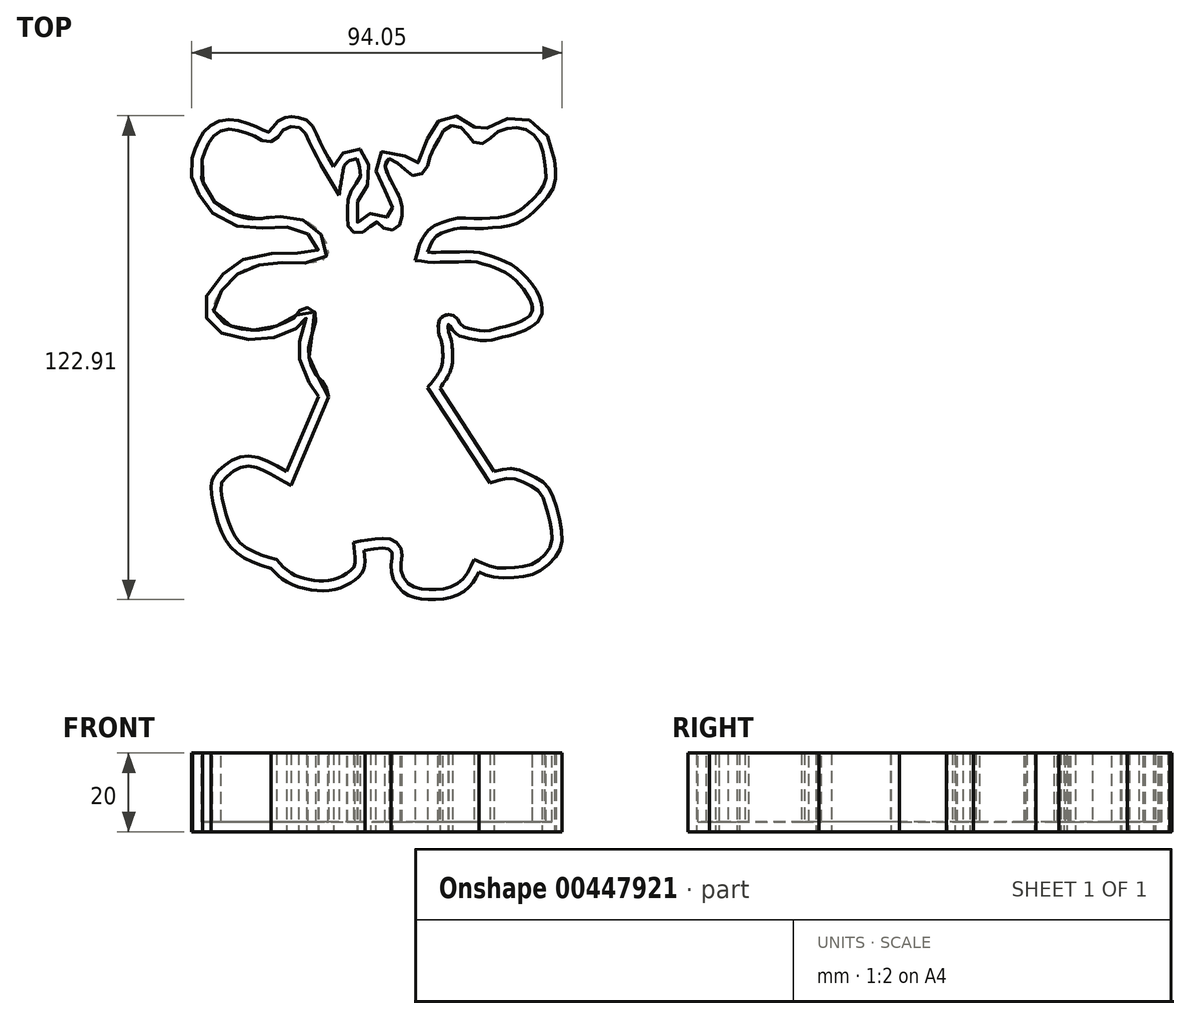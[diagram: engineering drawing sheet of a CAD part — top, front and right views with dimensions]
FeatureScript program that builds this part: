
annotation { "Feature Type Name" : "Feature", "Feature Type Description" : "" }
export const myFeature = defineFeature(function(context is Context, id is Id, definition is map)
    precondition{}
    {
        {
            var Q0;
            Q0=qCreatedBy(makeId("Top.planeOp"),FACE);
            var sketch = newSketch(context, id + "F0", { "sketchPlane" : qUnion([Q0])});
            skLineSegment(sketch, "E0", {"start": v(9.16, -14.18) * mm, "end": v(22.95, -35.4) * mm});
            skLineSegment(sketch, "E1", {"start": v(-21.7, -16.3) * mm, "end": v(-29.79, -35.4) * mm});
            skFitSpline(sketch, "E2", {"points": [v(-29.79, -35.4) * mm, v(-40.47, -31.51) * mm, v(-47.26, -35.4) * mm, v(-48.88, -38.63) * mm, v(-47.26, -48.01) * mm, v(-42.73, -55.78) * mm, v(-33.67, -59.99) * mm], "startDerivative": vector(-56.6, 32.87) * mm, "endDerivative": vector(55.84, -15.81) * mm});
            skFitSpline(sketch, "E3", {"points": [v(-33.67, -59.99) * mm, v(-30.11, -63.22) * mm, v(-23.32, -65.49) * mm, v(-16.85, -65.16) * mm, v(-12, -62.57) * mm, v(-10.05, -59.99) * mm, v(-10.05, -55.46) * mm], "startDerivative": vector(19.23, -21.63) * mm, "endDerivative": vector(-3.42, 31.7) * mm});
            skFitSpline(sketch, "E4", {"points": [v(-10.05, -55.46) * mm, v(-3.26, -55.46) * mm, v(-3.26, -60.3) * mm, v(0, -66.13) * mm, v(4.83, -67.75) * mm, v(11.63, -67.43) * mm, v(16.8, -64.52) * mm, v(19.07, -60.96) * mm], "startDerivative": vector(57.46, 10.07) * mm, "endDerivative": vector(14.9, 30.24) * mm});
            skFitSpline(sketch, "E5", {"points": [v(19.07, -60.96) * mm, v(22.67, -62.2) * mm, v(29.01, -62.2) * mm, v(34.09, -60.96) * mm, v(38.66, -56.94) * mm, v(40.18, -52.38) * mm, v(38.66, -44) * mm, v(36.12, -38.67) * mm, v(32.06, -36.13) * mm, v(27.49, -34.6) * mm, v(22.95, -35.4) * mm], "startDerivative": vector(38.82, -17.83) * mm, "endDerivative": vector(-49.39, -14.7) * mm});
            skFitSpline(sketch, "E6", {"points": [v(9.16, -14.18) * mm, v(11.9, -9.7) * mm, v(12.38, -4.83) * mm, v(11.37, 0) * mm], "startDerivative": vector(10.1, 12.56) * mm, "endDerivative": vector(-5.93, 12.01) * mm});
            skFitSpline(sketch, "E7", {"points": [v(11.37, 0) * mm, v(11.37, 2.02) * mm, v(12.86, 0) * mm, v(15.6, -1.32) * mm, v(20.38, -2.16) * mm, v(24.91, -1.32) * mm, v(29.45, 0) * mm, v(33.75, 2.38) * mm, v(35.06, 4.64) * mm], "startDerivative": vector(-3.42, 32.14) * mm, "endDerivative": vector(8.64, 21.84) * mm});
            skFitSpline(sketch, "E8", {"points": [v(35.06, 4.64) * mm, v(35.06, 7.27) * mm, v(33.03, 11.57) * mm, v(29.57, 15.5) * mm, v(25.99, 17.9) * mm, v(21.1, 19.68) * mm, v(18.11, 20.4) * mm, v(13.58, 20.4) * mm, v(10.12, 20.4) * mm, v(7.6, 20.28) * mm, v(6.06, 20.4) * mm], "startDerivative": vector(3.43, 29.15) * mm, "endDerivative": vector(-22.32, 2.7) * mm});
            skFitSpline(sketch, "E9", {"points": [v(6.06, 20.4) * mm, v(7.13, 22.9) * mm, v(8.74, 24.73) * mm, v(11.2, 25.77) * mm, v(14.05, 26.48) * mm, v(17.63, 26.36) * mm, v(23.12, 26.6) * mm, v(27.78, 27.32) * mm, v(31, 29) * mm, v(34.34, 31.85) * mm, v(38.28, 37.46) * mm, v(38.24, 43.73) * mm], "startDerivative": vector(9.98, 38.59) * mm, "endDerivative": vector(-9.06, 56.12) * mm});
            skFitSpline(sketch, "E10", {"points": [v(38.24, 43.73) * mm, v(37.02, 48.82) * mm, v(33.76, 52.86) * mm, v(29.88, 54.41) * mm, v(25.83, 54.26) * mm, v(21.8, 52.55) * mm, v(19.15, 50.37) * mm, v(17.75, 52.55) * mm, v(14.33, 54.72) * mm, v(11.06, 54.85) * mm, v(8.58, 53.32) * mm, v(6.87, 50.53) * mm, v(4.54, 46.02) * mm, v(3.14, 42.29) * mm, v(1.43, 43.73) * mm, v(-4.06, 46.67) * mm, v(-6.96, 43.73) * mm, v(-6.96, 40.73) * mm, v(-5.4, 37.16) * mm, v(-3.85, 34.36) * mm, v(-2.92, 31.72) * mm, v(-3.38, 28.46) * mm, v(-4.94, 29.86) * mm, v(-7.73, 30.48) * mm, v(-9.6, 29.39) * mm, v(-11.62, 27.68) * mm, v(-11.77, 30.78) * mm, v(-11.62, 33.87) * mm, v(-9.77, 36.64) * mm, v(-8.53, 39.11) * mm, v(-9.15, 43.73) * mm, v(-10.39, 46.36) * mm, v(-12.55, 46.52) * mm, v(-15.01, 45.75) * mm, v(-17.17, 43.73) * mm, v(-17.8, 42.04) * mm], "startDerivative": vector(-20.73, 146.47) * mm, "endDerivative": vector(-14.6, -87.54) * mm});
            skFitSpline(sketch, "E11", {"points": [v(-17.8, 42.04) * mm, v(-20.26, 46.36) * mm, v(-22.11, 50.22) * mm, v(-24.27, 53.62) * mm, v(-27.51, 54.7) * mm, v(-29.83, 54.7) * mm, v(-32.6, 53) * mm, v(-34.3, 50.84) * mm, v(-36, 51.6) * mm, v(-39.4, 53) * mm, v(-44.33, 54.08) * mm, v(-49.11, 52.54) * mm, v(-52.04, 48.83) * mm, v(-53.74, 44.2) * mm], "startDerivative": vector(-29.56, 49.97) * mm, "endDerivative": vector(-16.76, -54.28) * mm});
            skFitSpline(sketch, "E12", {"points": [v(-53.74, 44.2) * mm, v(-53.74, 41.12) * mm, v(-53.74, 38.03) * mm, v(-52.2, 35.25) * mm, v(-50.04, 31.55) * mm, v(-44.64, 28) * mm, v(-39.08, 26.3) * mm, v(-33.22, 26.77) * mm, v(-28.44, 26.61) * mm, v(-24.43, 25.07) * mm, v(-22.42, 22.14) * mm, v(-21.8, 20.6) * mm, v(-26.59, 20.13) * mm, v(-32.3, 20.13) * mm, v(-39.86, 18.9) * mm, v(-44.48, 16.12) * mm, v(-48.34, 11.96) * mm, v(-51.12, 6.1) * mm, v(-49.27, 2.54) * mm, v(-46.64, 0) * mm, v(-40.32, -1.78) * mm, v(-34.15, -1.62) * mm, v(-29.52, 0) * mm, v(-25.66, 2.24) * mm, v(-24.74, 3.78) * mm, v(-25.82, 0) * mm, v(-26.74, -3.94) * mm, v(-26.59, -6.25) * mm, v(-24.89, -11.65) * mm, v(-22.42, -14.43) * mm, v(-21.7, -16.3) * mm], "startDerivative": vector(3.92, -108.76) * mm, "endDerivative": vector(23.6, -82.05) * mm});
            skSolve(sketch);
        }
        {
            var Q0;
            Q0=makeQuery(id+"F0.imprint","IMPRINT",FACE,{"disambiguationData":[TD([[makeQuery(id+"F0.imprint","IMPRINT",EDGE,{"derivedFrom":sQuery(id+"F0.wireOp",EDGE,"E0")}),-1.0]])]});
            extrude(context, id + "F1", {"entities" : qUnion([Q0]), "depth" : 20 * mm, "offsetDistance" : 25 * mm});
        }
        {
            var Q0;
            Q0=makeQuery(id+"F1.opExtrude","CAP_FACE",FACE,{"disambiguationData":[OSD([sQuery(id+"F0.wireOp",EDGE,"E0"),sQuery(id+"F0.wireOp",EDGE,"E1"),sQuery(id+"F0.wireOp",EDGE,"E2"),sQuery(id+"F0.wireOp",EDGE,"E3"),sQuery(id+"F0.wireOp",EDGE,"E4"),sQuery(id+"F0.wireOp",EDGE,"E5"),sQuery(id+"F0.wireOp",EDGE,"E6"),sQuery(id+"F0.wireOp",EDGE,"E7"),sQuery(id+"F0.wireOp",EDGE,"E8"),sQuery(id+"F0.wireOp",EDGE,"E9"),sQuery(id+"F0.wireOp",EDGE,"E10"),sQuery(id+"F0.wireOp",EDGE,"E11"),sQuery(id+"F0.wireOp",EDGE,"E12")])],"isStart":false});
            shell(context, id + "F2", {"entities" : qUnion([Q0]), "thickness" : 2.5 * mm});
        }
    });
